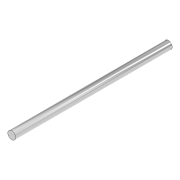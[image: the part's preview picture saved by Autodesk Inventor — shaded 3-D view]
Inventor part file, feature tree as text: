
AUTODESK INVENTOR PART (.ipt)
format: ipt  version: 2020 (Build 240168000, 168)  size: 72,704 bytes
history: native  units: in
note: dims shown in document units (in); Inventor stores cm internally (conversion verified against a paired STEP export)
features: extrude x1, sketch x1
ambient origin geometry x8: Origin, YZ Plane, XZ Plane, XY Plane, X Axis, Y Axis, Z Axis, Center Point
bodies: Solid1 (feature_tree)
feature tree (2):
  extrude  "Extrusion1"  Depth=3.937in TaperAngle=0.0deg
  sketch  "Sketch1"  dims[d0=0.1969in d1=3.937in d2=0.0in]
